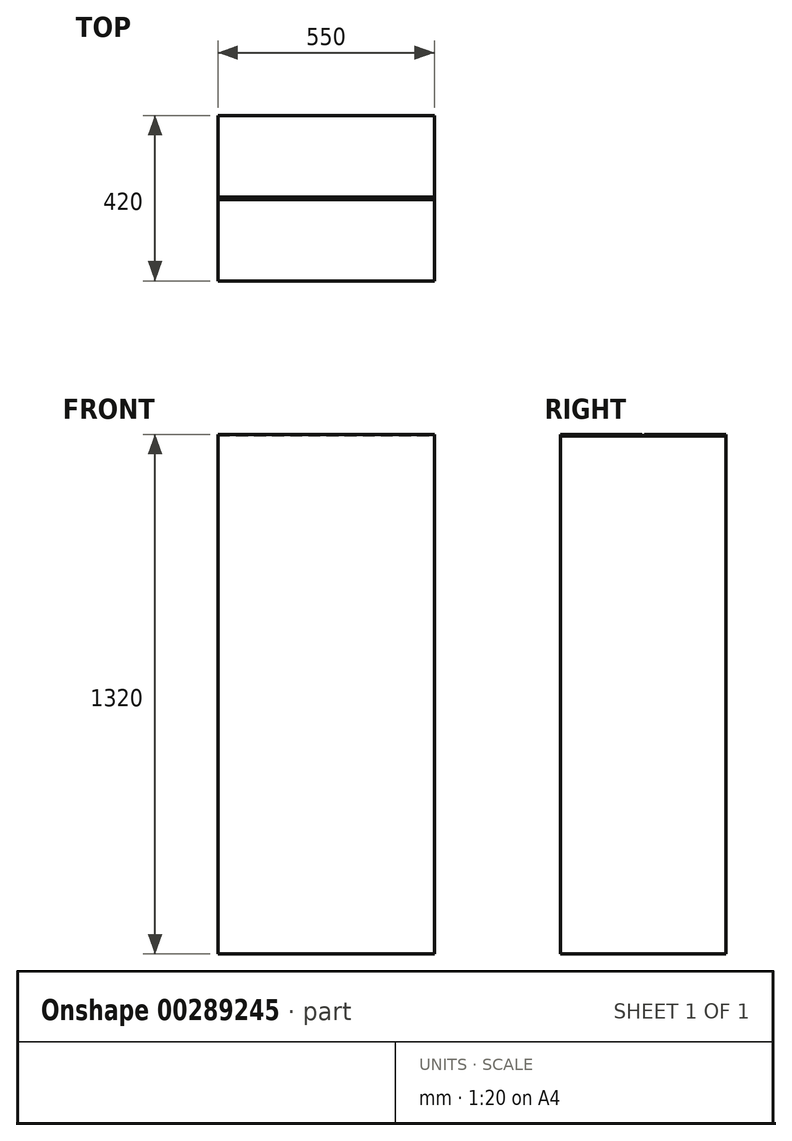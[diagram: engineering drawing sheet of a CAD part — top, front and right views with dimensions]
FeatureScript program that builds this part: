
annotation { "Feature Type Name" : "Feature", "Feature Type Description" : "" }
export const myFeature = defineFeature(function(context is Context, id is Id, definition is map)
    precondition{}
    {
        {
            var Q0;
            Q0=qCreatedBy(makeId("Top.planeOp"),FACE);
            var sketch = newSketch(context, id + "F0", { "sketchPlane" : qUnion([Q0])});
            skLineSegment(sketch, "E0.bottom", {"start": v(275, -210) * mm, "end": v(-275, -210) * mm});
            skLineSegment(sketch, "E0.top", {"start": v(275, 210) * mm, "end": v(-275, 210) * mm});
            skLineSegment(sketch, "E0.left", {"start": v(275, -210) * mm, "end": v(275, 210) * mm});
            skLineSegment(sketch, "E0.right", {"start": v(-275, -210) * mm, "end": v(-275, 210) * mm});
            skPoint(sketch, "E0.middle", {"position": v(0, 0) * mm});
            skSolve(sketch);
        }
        {
            var Q0;
            Q0 = qSketchRegion(id + "F0", true);
            extrude(context, id + "F1", {"entities" : qUnion([Q0]), "depth" : 1320 * mm});
        }
        {
            var Q0;
            Q0=makeQuery(id+"F1.opExtrude","SWEPT_FACE",FACE,{"disambiguationData":[OSD([sQuery(id+"F0.wireOp",EDGE,"E0.left")])]});
            var sketch = newSketch(context, id + "F2", { "sketchPlane" : qUnion([Q0])});
            skLineSegment(sketch, "E1", {"start": v(0, 1320) * mm, "end": v(0, 1336.15) * mm, "construction": true});
            skPoint(sketch, "E1.endSnap0", {"position": v(0, 1320) * mm});
            skLineSegment(sketch, "E2.bottom", {"start": v(3, 1317.5) * mm, "end": v(-3, 1317.5) * mm});
            skLineSegment(sketch, "E2.top", {"start": v(3, 1322.5) * mm, "end": v(-3, 1322.5) * mm});
            skLineSegment(sketch, "E2.left", {"start": v(3, 1317.5) * mm, "end": v(3, 1322.5) * mm});
            skLineSegment(sketch, "E2.right", {"start": v(-3, 1317.5) * mm, "end": v(-3, 1322.5) * mm});
            skSolve(sketch);
        }
        {
            var Q0;
            Q0 = qSketchRegion(id + "F2", true);
            extrude(context, id + "F3", {"entities" : qUnion([Q0]), "operationType" : NewBodyOperationType.REMOVE, "endBound" : BoundingType.THROUGH_ALL, "oppositeDirection" : true, "depth" : 25 * mm});
        }
        {
            var Q0;
            Q0=makeQuery(id+"F1.opExtrude","SWEPT_FACE",FACE,{"disambiguationData":[OSD([sQuery(id+"F0.wireOp",EDGE,"E0.left")])]});
            var sketch = newSketch(context, id + "F4", { "sketchPlane" : qUnion([Q0])});
            skLineSegment(sketch, "E3.bottom", {"start": v(208.47, 1315.62) * mm, "end": v(-208.47, 1315.62) * mm});
            skLineSegment(sketch, "E3.top", {"start": v(208.47, 1317.5) * mm, "end": v(-208.47, 1317.5) * mm});
            skLineSegment(sketch, "E3.left", {"start": v(208.47, 1315.62) * mm, "end": v(208.47, 1317.5) * mm});
            skLineSegment(sketch, "E3.right", {"start": v(-208.47, 1315.62) * mm, "end": v(-208.47, 1317.5) * mm});
            skPoint(sketch, "E3.middle", {"position": v(0, 1316.56) * mm});
            skSolve(sketch);
        }
        {
            var Q0;
            Q0 = qSketchRegion(id + "F4", true);
            extrude(context, id + "F5", {"entities" : qUnion([Q0]), "operationType" : NewBodyOperationType.REMOVE, "oppositeDirection" : true, "depth" : 2 * mm});
        }
    });
